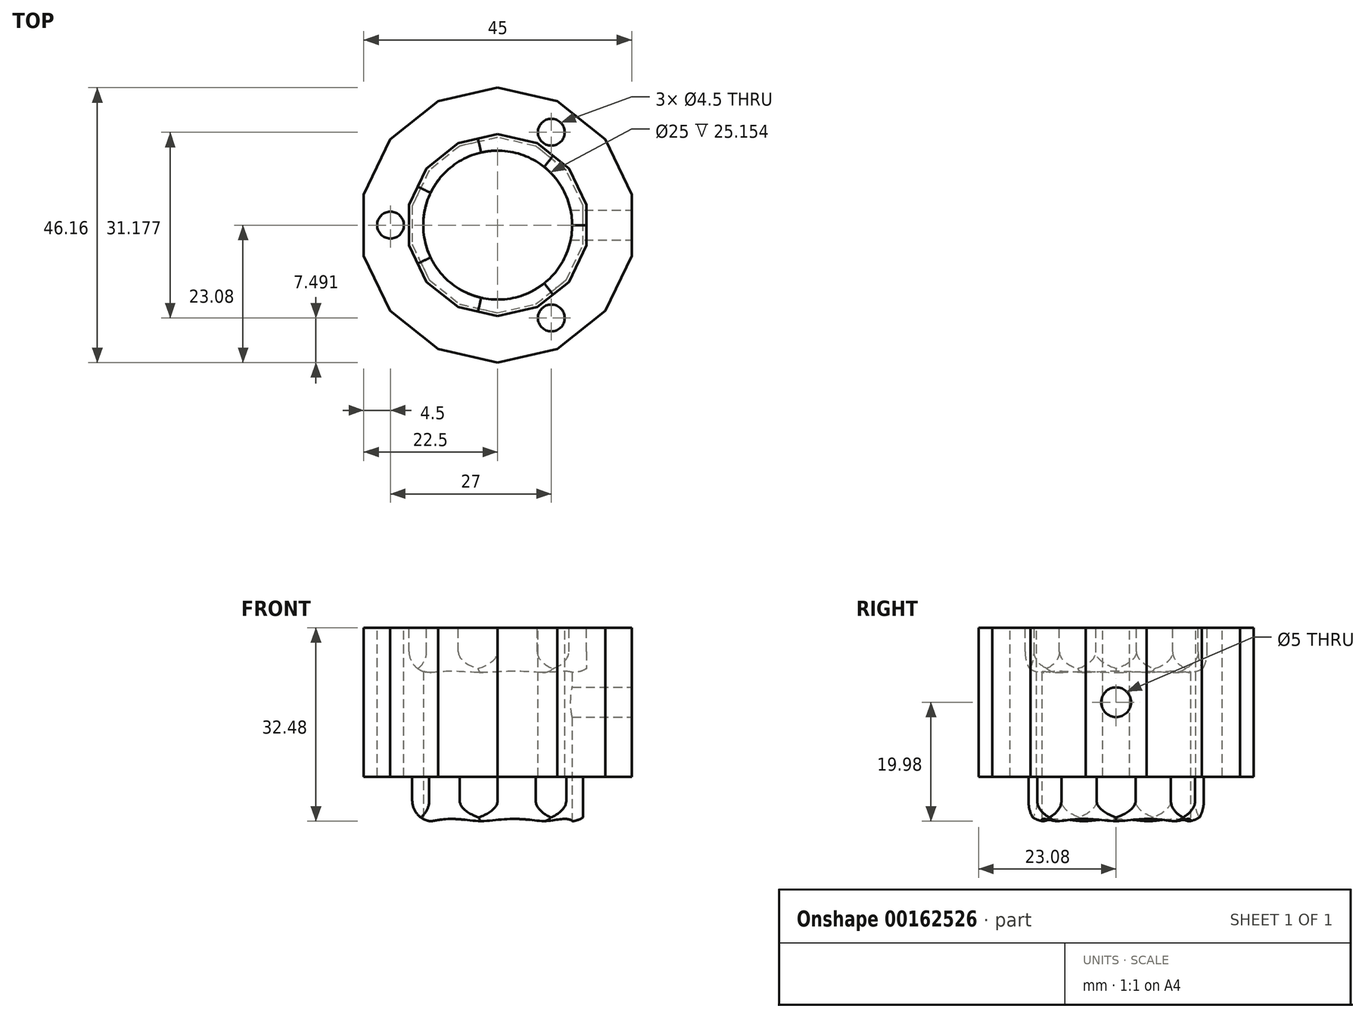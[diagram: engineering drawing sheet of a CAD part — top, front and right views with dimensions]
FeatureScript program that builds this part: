
annotation { "Feature Type Name" : "Feature", "Feature Type Description" : "" }
export const myFeature = defineFeature(function(context is Context, id is Id, definition is map)
    precondition{}
    {
        {
            var Q0;
            Q0=qCreatedBy(makeId("Top.planeOp"),FACE);
            var sketch = newSketch(context, id + "F0", { "sketchPlane" : qUnion([Q0])});
            skCircle(sketch, "E0", {"center": v(0, 0) * mm, "radius": 12.5 * mm});
            skCircle(sketch, "E1.cCircle", {"center": v(0, 0) * mm, "radius": 17.5 * mm, "construction": true});
            skLineSegment(sketch, "E1.0", {"start": v(17.5, 8.43) * mm, "end": v(17.5, -8.43) * mm, "construction": true});
            skLineSegment(sketch, "E1.1", {"start": v(17.5, -8.43) * mm, "end": v(4.32, -18.94) * mm, "construction": true});
            skLineSegment(sketch, "E1.2", {"start": v(4.32, -18.94) * mm, "end": v(-12.11, -15.19) * mm, "construction": true});
            skLineSegment(sketch, "E1.3", {"start": v(-12.11, -15.19) * mm, "end": v(-19.42, 0) * mm, "construction": true});
            skLineSegment(sketch, "E1.4", {"start": v(-19.42, 0) * mm, "end": v(-12.11, 15.19) * mm, "construction": true});
            skLineSegment(sketch, "E1.5", {"start": v(-12.11, 15.19) * mm, "end": v(4.32, 18.94) * mm, "construction": true});
            skLineSegment(sketch, "E1.6", {"start": v(4.32, 18.94) * mm, "end": v(17.5, 8.43) * mm, "construction": true});
            skPoint(sketch, "E1.0.midPoint", {"position": v(17.5, 0) * mm});
            skArc(sketch, "E2", {"start": v(7.16, 16.67) * mm, "mid": v(13.9, 17.43) * mm, "end": v(14.66, 10.69) * mm, "construction": true});
            skArc(sketch, "E3", {"start": v(0.79, 18.13) * mm, "mid": v(-4.96, 21.74) * mm, "end": v(-8.57, 16) * mm, "construction": true});
            skArc(sketch, "E4", {"start": v(-13.68, 11.92) * mm, "mid": v(-20.1, 9.68) * mm, "end": v(-17.85, 3.27) * mm, "construction": true});
            skArc(sketch, "E5", {"start": v(-17.85, -3.27) * mm, "mid": v(-20.1, -9.68) * mm, "end": v(-13.68, -11.92) * mm, "construction": true});
            skArc(sketch, "E6", {"start": v(-8.57, -16) * mm, "mid": v(-4.96, -21.74) * mm, "end": v(0.79, -18.13) * mm, "construction": true});
            skArc(sketch, "E7", {"start": v(14.66, -10.69) * mm, "mid": v(13.9, -17.43) * mm, "end": v(7.16, -16.67) * mm, "construction": true});
            skCircle(sketch, "E8.cCircle", {"center": v(0, 0) * mm, "radius": 22.5 * mm, "construction": true});
            skLineSegment(sketch, "E8.0", {"start": v(22.5, 5.14) * mm, "end": v(22.5, -5.14) * mm});
            skLineSegment(sketch, "E8.1", {"start": v(22.5, -5.14) * mm, "end": v(18.04, -14.39) * mm});
            skLineSegment(sketch, "E8.2", {"start": v(18.04, -14.39) * mm, "end": v(10.01, -20.8) * mm});
            skLineSegment(sketch, "E8.3", {"start": v(10.01, -20.8) * mm, "end": v(0, -23.08) * mm});
            skLineSegment(sketch, "E8.4", {"start": v(0, -23.08) * mm, "end": v(-10.01, -20.8) * mm});
            skLineSegment(sketch, "E8.5", {"start": v(-10.01, -20.8) * mm, "end": v(-18.04, -14.39) * mm});
            skLineSegment(sketch, "E8.6", {"start": v(-18.04, -14.39) * mm, "end": v(-22.5, -5.14) * mm});
            skLineSegment(sketch, "E8.7", {"start": v(-22.5, -5.14) * mm, "end": v(-22.5, 5.14) * mm});
            skLineSegment(sketch, "E8.8", {"start": v(-22.5, 5.14) * mm, "end": v(-18.04, 14.39) * mm});
            skLineSegment(sketch, "E8.9", {"start": v(-18.04, 14.39) * mm, "end": v(-10.01, 20.8) * mm});
            skLineSegment(sketch, "E8.10", {"start": v(-10.01, 20.8) * mm, "end": v(0, 23.08) * mm});
            skLineSegment(sketch, "E8.11", {"start": v(0, 23.08) * mm, "end": v(10.01, 20.8) * mm});
            skLineSegment(sketch, "E8.12", {"start": v(10.01, 20.8) * mm, "end": v(18.04, 14.39) * mm});
            skLineSegment(sketch, "E8.13", {"start": v(18.04, 14.39) * mm, "end": v(22.5, 5.14) * mm});
            skPoint(sketch, "E8.0.midPoint", {"position": v(22.5, 0) * mm});
            skSolve(sketch);
        }
        {
            var Q0;
            Q0=qSketchRegion(id+"F0",true);
            extrude(context, id + "F1", {"entities" : qUnion([Q0]), "endBound" : BoundingType.SYMMETRIC, "depth" : 25 * mm, "offsetDistance" : 25 * mm});
        }
        {
            var Q0;
            Q0=makeQuery(id+"F1.opExtrude","CAP_FACE",FACE,{"disambiguationData":[OSD([sQuery(id+"F0.wireOp",EDGE,"E0"),sQuery(id+"F0.wireOp",EDGE,"E1.0"),sQuery(id+"F0.wireOp",EDGE,"E1.1"),sQuery(id+"F0.wireOp",EDGE,"E1.2"),sQuery(id+"F0.wireOp",EDGE,"E1.3"),sQuery(id+"F0.wireOp",EDGE,"E1.4"),sQuery(id+"F0.wireOp",EDGE,"E1.5"),sQuery(id+"F0.wireOp",EDGE,"E1.6"),sQuery(id+"F0.wireOp",EDGE,"E2"),sQuery(id+"F0.wireOp",EDGE,"E3"),sQuery(id+"F0.wireOp",EDGE,"E4"),sQuery(id+"F0.wireOp",EDGE,"E5"),sQuery(id+"F0.wireOp",EDGE,"E6"),sQuery(id+"F0.wireOp",EDGE,"E7")])],"isStart":false});
            var sketch = newSketch(context, id + "F2", { "sketchPlane" : qUnion([Q0])});
            skLineSegment(sketch, "E9", {"start": v(0, 0) * mm, "end": v(11.38, 19.7) * mm, "construction": true});
            skCircle(sketch, "E10", {"center": v(9, 15.59) * mm, "radius": 2.25 * mm});
            skCircle(sketch, "E11.1.0", {"center": v(-18, 0) * mm, "radius": 2.25 * mm});
            skCircle(sketch, "E11.2.0", {"center": v(9, -15.59) * mm, "radius": 2.25 * mm});
            skPoint(sketch, "E11.center", {"position": v(0, 0) * mm});
            skSolve(sketch);
        }
        {
            var Q0;
            Q0=qSketchRegion(id+"F2",true);
            extrude(context, id + "F3", {"entities" : qUnion([Q0]), "operationType" : NewBodyOperationType.REMOVE, "oppositeDirection" : true, "depth" : 25 * mm, "offsetDistance" : 25 * mm});
        }
        {
            var Q0;
            Q0=makeQuery(id+"F1.opExtrude","CAP_FACE",FACE,{"disambiguationData":[OSD([sQuery(id+"F0.wireOp",EDGE,"E0"),sQuery(id+"F0.wireOp",EDGE,"E1.0"),sQuery(id+"F0.wireOp",EDGE,"E1.1"),sQuery(id+"F0.wireOp",EDGE,"E1.2"),sQuery(id+"F0.wireOp",EDGE,"E1.3"),sQuery(id+"F0.wireOp",EDGE,"E1.4"),sQuery(id+"F0.wireOp",EDGE,"E1.5"),sQuery(id+"F0.wireOp",EDGE,"E1.6"),sQuery(id+"F0.wireOp",EDGE,"E2"),sQuery(id+"F0.wireOp",EDGE,"E3"),sQuery(id+"F0.wireOp",EDGE,"E4"),sQuery(id+"F0.wireOp",EDGE,"E5"),sQuery(id+"F0.wireOp",EDGE,"E6"),sQuery(id+"F0.wireOp",EDGE,"E7")])],"isStart":false});
            var sketch = newSketch(context, id + "F4", { "sketchPlane" : qUnion([Q0])});
            skCircle(sketch, "E12", {"center": v(0, 0) * mm, "radius": 12.5 * mm});
            skCircle(sketch, "E13.cCircle", {"center": v(0, 0) * mm, "radius": 14.9 * mm, "construction": true});
            skLineSegment(sketch, "E13.0", {"start": v(14.9, 3.4) * mm, "end": v(14.9, -3.4) * mm});
            skLineSegment(sketch, "E13.1", {"start": v(14.9, -3.4) * mm, "end": v(11.95, -9.53) * mm});
            skLineSegment(sketch, "E13.2", {"start": v(11.95, -9.53) * mm, "end": v(6.63, -13.77) * mm});
            skLineSegment(sketch, "E13.3", {"start": v(6.63, -13.77) * mm, "end": v(0, -15.28) * mm});
            skLineSegment(sketch, "E13.4", {"start": v(0, -15.28) * mm, "end": v(-6.63, -13.77) * mm});
            skLineSegment(sketch, "E13.5", {"start": v(-6.63, -13.77) * mm, "end": v(-11.95, -9.53) * mm});
            skLineSegment(sketch, "E13.6", {"start": v(-11.95, -9.53) * mm, "end": v(-14.9, -3.4) * mm});
            skLineSegment(sketch, "E13.7", {"start": v(-14.9, -3.4) * mm, "end": v(-14.9, 3.4) * mm});
            skLineSegment(sketch, "E13.8", {"start": v(-14.9, 3.4) * mm, "end": v(-11.95, 9.53) * mm});
            skLineSegment(sketch, "E13.9", {"start": v(-11.95, 9.53) * mm, "end": v(-6.63, 13.77) * mm});
            skLineSegment(sketch, "E13.10", {"start": v(-6.63, 13.77) * mm, "end": v(0, 15.28) * mm});
            skLineSegment(sketch, "E13.11", {"start": v(0, 15.28) * mm, "end": v(6.63, 13.77) * mm});
            skLineSegment(sketch, "E13.12", {"start": v(6.63, 13.77) * mm, "end": v(11.95, 9.53) * mm});
            skLineSegment(sketch, "E13.13", {"start": v(11.95, 9.53) * mm, "end": v(14.9, 3.4) * mm});
            skPoint(sketch, "E13.0.midPoint", {"position": v(14.9, 0) * mm});
            skSolve(sketch);
        }
        {
            var Q0;
            Q0=qSketchRegion(id+"F4",true);
            extrude(context, id + "F5", {"entities" : qUnion([Q0]), "operationType" : NewBodyOperationType.REMOVE, "oppositeDirection" : true, "depth" : 7.5 * mm, "offsetDistance" : 25 * mm});
        }
        {
            var Q0;
            Q0=makeQuery(id+"F1.opExtrude","CAP_FACE",FACE,{"disambiguationData":[OSD([sQuery(id+"F0.wireOp",EDGE,"E0"),sQuery(id+"F0.wireOp",EDGE,"E1.0"),sQuery(id+"F0.wireOp",EDGE,"E1.1"),sQuery(id+"F0.wireOp",EDGE,"E1.2"),sQuery(id+"F0.wireOp",EDGE,"E1.3"),sQuery(id+"F0.wireOp",EDGE,"E1.4"),sQuery(id+"F0.wireOp",EDGE,"E1.5"),sQuery(id+"F0.wireOp",EDGE,"E1.6"),sQuery(id+"F0.wireOp",EDGE,"E2"),sQuery(id+"F0.wireOp",EDGE,"E3"),sQuery(id+"F0.wireOp",EDGE,"E4"),sQuery(id+"F0.wireOp",EDGE,"E5"),sQuery(id+"F0.wireOp",EDGE,"E6"),sQuery(id+"F0.wireOp",EDGE,"E7")])],"isStart":true});
            var sketch = newSketch(context, id + "F6", { "sketchPlane" : qUnion([Q0])});
            skCircle(sketch, "E14", {"center": v(0, 0) * mm, "radius": 12.5 * mm});
            skCircle(sketch, "E15.cCircle", {"center": v(0, 0) * mm, "radius": 14.35 * mm, "construction": true});
            skLineSegment(sketch, "E15.0", {"start": v(14.35, 3.28) * mm, "end": v(14.35, -3.28) * mm});
            skLineSegment(sketch, "E15.1", {"start": v(14.35, -3.28) * mm, "end": v(11.5, -9.18) * mm});
            skLineSegment(sketch, "E15.2", {"start": v(11.5, -9.18) * mm, "end": v(6.39, -13.26) * mm});
            skLineSegment(sketch, "E15.3", {"start": v(6.39, -13.26) * mm, "end": v(0, -14.72) * mm});
            skLineSegment(sketch, "E15.4", {"start": v(0, -14.72) * mm, "end": v(-6.39, -13.26) * mm});
            skLineSegment(sketch, "E15.5", {"start": v(-6.39, -13.26) * mm, "end": v(-11.5, -9.18) * mm});
            skLineSegment(sketch, "E15.6", {"start": v(-11.5, -9.18) * mm, "end": v(-14.35, -3.28) * mm});
            skLineSegment(sketch, "E15.7", {"start": v(-14.35, -3.28) * mm, "end": v(-14.35, 3.28) * mm});
            skLineSegment(sketch, "E15.8", {"start": v(-14.35, 3.28) * mm, "end": v(-11.5, 9.18) * mm});
            skLineSegment(sketch, "E15.9", {"start": v(-11.5, 9.18) * mm, "end": v(-6.39, 13.26) * mm});
            skLineSegment(sketch, "E15.10", {"start": v(-6.39, 13.26) * mm, "end": v(0, 14.72) * mm});
            skLineSegment(sketch, "E15.11", {"start": v(0, 14.72) * mm, "end": v(6.39, 13.26) * mm});
            skLineSegment(sketch, "E15.12", {"start": v(6.39, 13.26) * mm, "end": v(11.5, 9.18) * mm});
            skLineSegment(sketch, "E15.13", {"start": v(11.5, 9.18) * mm, "end": v(14.35, 3.28) * mm});
            skPoint(sketch, "E15.0.midPoint", {"position": v(14.35, 0) * mm});
            skSolve(sketch);
        }
        {
            var Q0;
            Q0=qSketchRegion(id+"F6",true);
            extrude(context, id + "F7", {"entities" : qUnion([Q0]), "operationType" : NewBodyOperationType.ADD, "depth" : 7.5 * mm, "offsetDistance" : 25 * mm});
        }
        {
            var Q0;
            Q0=makeQuery(id+"F5.boolean.opBoolean","COPY",EDGE,{"derivedFrom":makeQuery(id+"F5.opExtrude","CAP_EDGE",EDGE,{"disambiguationData":[OSD([sQuery(id+"F4.wireOp",EDGE,"E13.9")])],"isStart":false})});
            var Q1;
            Q1=makeQuery(id+"F5.boolean.opBoolean","COPY",EDGE,{"derivedFrom":makeQuery(id+"F5.opExtrude","CAP_EDGE",EDGE,{"disambiguationData":[OSD([sQuery(id+"F4.wireOp",EDGE,"E13.7")])],"isStart":false})});
            var Q2;
            Q2=makeQuery(id+"F5.boolean.opBoolean","COPY",EDGE,{"derivedFrom":makeQuery(id+"F5.opExtrude","CAP_EDGE",EDGE,{"disambiguationData":[OSD([sQuery(id+"F4.wireOp",EDGE,"E13.5")])],"isStart":false})});
            var Q3;
            Q3=makeQuery(id+"F5.boolean.opBoolean","COPY",EDGE,{"derivedFrom":makeQuery(id+"F5.opExtrude","CAP_EDGE",EDGE,{"disambiguationData":[OSD([sQuery(id+"F4.wireOp",EDGE,"E13.3")])],"isStart":false})});
            var Q4;
            Q4=makeQuery(id+"F5.boolean.opBoolean","COPY",EDGE,{"derivedFrom":makeQuery(id+"F5.opExtrude","CAP_EDGE",EDGE,{"disambiguationData":[OSD([sQuery(id+"F4.wireOp",EDGE,"E13.1")])],"isStart":false})});
            var Q5;
            Q5=makeQuery(id+"F5.boolean.opBoolean","COPY",EDGE,{"derivedFrom":makeQuery(id+"F5.opExtrude","CAP_EDGE",EDGE,{"disambiguationData":[OSD([sQuery(id+"F4.wireOp",EDGE,"E13.13")])],"isStart":false})});
            var Q6;
            Q6=makeQuery(id+"F5.boolean.opBoolean","COPY",EDGE,{"derivedFrom":makeQuery(id+"F5.opExtrude","CAP_EDGE",EDGE,{"disambiguationData":[OSD([sQuery(id+"F4.wireOp",EDGE,"E13.11")])],"isStart":false})});
            fillet(context, id + "F8", {"entities" : qUnion([Q0, Q1, Q2, Q3, Q4, Q5, Q6]), "radius" : 3.5 * mm, "tangentPropagation" : true, "allowEdgeOverflow" : false});
        }
        {
            var Q0;
            Q0=makeQuery(id+"F7.opExtrude","CAP_EDGE",EDGE,{"disambiguationData":[OSD([sQuery(id+"F6.wireOp",EDGE,"E15.1")])],"isStart":false});
            var Q1;
            Q1=makeQuery(id+"F7.opExtrude","CAP_EDGE",EDGE,{"disambiguationData":[OSD([sQuery(id+"F6.wireOp",EDGE,"E15.3")])],"isStart":false});
            var Q2;
            Q2=makeQuery(id+"F7.opExtrude","CAP_EDGE",EDGE,{"disambiguationData":[OSD([sQuery(id+"F6.wireOp",EDGE,"E15.5")])],"isStart":false});
            var Q3;
            Q3=makeQuery(id+"F7.opExtrude","CAP_EDGE",EDGE,{"disambiguationData":[OSD([sQuery(id+"F6.wireOp",EDGE,"E15.7")])],"isStart":false});
            var Q4;
            Q4=makeQuery(id+"F7.opExtrude","CAP_EDGE",EDGE,{"disambiguationData":[OSD([sQuery(id+"F6.wireOp",EDGE,"E15.9")])],"isStart":false});
            var Q5;
            Q5=makeQuery(id+"F7.opExtrude","CAP_EDGE",EDGE,{"disambiguationData":[OSD([sQuery(id+"F6.wireOp",EDGE,"E15.11")])],"isStart":false});
            var Q6;
            Q6=makeQuery(id+"F7.opExtrude","CAP_EDGE",EDGE,{"disambiguationData":[OSD([sQuery(id+"F6.wireOp",EDGE,"E15.13")])],"isStart":false});
            fillet(context, id + "F9", {"entities" : qUnion([Q0, Q1, Q2, Q3, Q4, Q5, Q6]), "radius" : 3.5 * mm, "allowEdgeOverflow" : false});
        }
        {
            var Q0;
            Q0=makeQuery(id+"F1.opExtrude","SWEPT_FACE",FACE,{"disambiguationData":[OSD([sQuery(id+"F0.wireOp",EDGE,"E8.0")])]});
            var sketch = newSketch(context, id + "F10", { "sketchPlane" : qUnion([Q0])});
            skCircle(sketch, "E16", {"center": v(0, 0) * mm, "radius": 2.5 * mm});
            skSolve(sketch);
        }
        {
            var Q0;
            Q0 = qSketchRegion(id + "F10", true);
            extrude(context, id + "F11", {"entities" : qUnion([Q0]), "operationType" : NewBodyOperationType.REMOVE, "oppositeDirection" : true, "depth" : 12 * mm, "offsetDistance" : 25 * mm});
        }
    });
